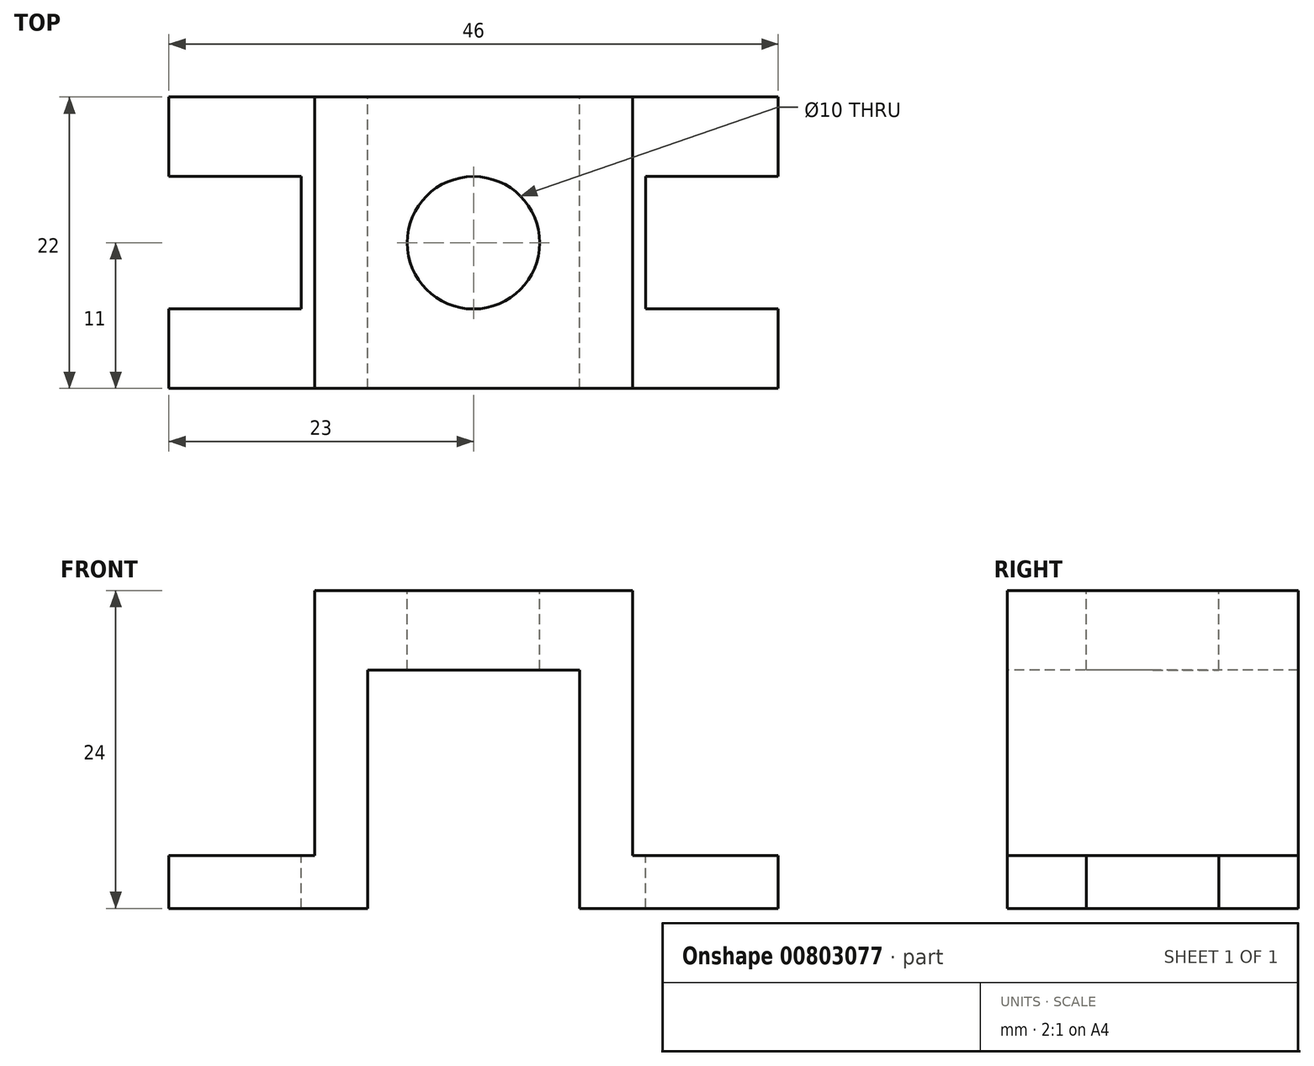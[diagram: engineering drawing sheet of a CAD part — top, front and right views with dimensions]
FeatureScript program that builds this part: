
annotation { "Feature Type Name" : "Feature", "Feature Type Description" : "" }
export const myFeature = defineFeature(function(context is Context, id is Id, definition is map)
    precondition{}
    {
        {
            var Q0;
            Q0=qCreatedBy(makeId("Front.planeOp"),FACE);
            var sketch = newSketch(context, id + "F0", { "sketchPlane" : qUnion([Q0])});
            skLineSegment(sketch, "E0.bottom", {"start": v(23, 12) * mm, "end": v(-23, 12) * mm});
            skLineSegment(sketch, "E0.top", {"start": v(23, -12) * mm, "end": v(-23, -12) * mm});
            skLineSegment(sketch, "E0.left", {"start": v(23, 12) * mm, "end": v(23, -12) * mm});
            skLineSegment(sketch, "E0.right", {"start": v(-23, 12) * mm, "end": v(-23, -12) * mm});
            skPoint(sketch, "E0.middle", {"position": v(0, 0) * mm});
            skSolve(sketch);
        }
        {
            var Q0;
            Q0 = qSketchRegion(id + "F0", true);
            extrude(context, id + "F1", {"entities" : qUnion([Q0]), "depth" : 11 * mm, "offsetDistance" : 25 * mm, "hasSecondDirection" : true, "secondDirectionOppositeDirection" : true, "secondDirectionDepth" : 11 * mm});
        }
        {
            var Q0;
            Q0=qCreatedBy(makeId("Front.planeOp"),FACE);
            var sketch = newSketch(context, id + "F2", { "sketchPlane" : qUnion([Q0])});
            skLineSegment(sketch, "E1.bottom", {"start": v(-8, 6) * mm, "end": v(8, 6) * mm});
            skLineSegment(sketch, "E1.top", {"start": v(-8, -21.9) * mm, "end": v(8, -21.9) * mm});
            skLineSegment(sketch, "E1.left", {"start": v(-8, 6) * mm, "end": v(-8, -21.9) * mm});
            skLineSegment(sketch, "E1.right", {"start": v(8, 6) * mm, "end": v(8, -21.9) * mm});
            skLineSegment(sketch, "E2.bottom", {"start": v(-28.7, 14) * mm, "end": v(-12, 14) * mm});
            skLineSegment(sketch, "E2.top", {"start": v(-28.7, -8) * mm, "end": v(-12, -8) * mm});
            skLineSegment(sketch, "E2.left", {"start": v(-28.7, 14) * mm, "end": v(-28.7, -8) * mm});
            skLineSegment(sketch, "E2.right", {"start": v(-12, 14) * mm, "end": v(-12, -8) * mm});
            skLineSegment(sketch, "E3.MirrorCS", {"start": v(12, 14) * mm, "end": v(12, -8) * mm});
            skLineSegment(sketch, "E4.MirrorCS", {"start": v(28.7, -8) * mm, "end": v(12, -8) * mm});
            skLineSegment(sketch, "E5.MirrorCS", {"start": v(28.7, 14) * mm, "end": v(28.7, -8) * mm});
            skLineSegment(sketch, "E6.MirrorCS", {"start": v(28.7, 14) * mm, "end": v(12, 14) * mm});
            skSolve(sketch);
        }
        {
            var Q0;
            Q0=makeQuery(id+"F2.imprint","IMPRINT",FACE,{"disambiguationData":[TD([[makeQuery(id+"F2.imprint","IMPRINT",EDGE,{"derivedFrom":sQuery(id+"F2.wireOp",EDGE,"E2.bottom")}),-1.0]])]});
            var Q1;
            Q1=makeQuery(id+"F2.imprint","IMPRINT",FACE,{"disambiguationData":[TD([[makeQuery(id+"F2.imprint","IMPRINT",EDGE,{"derivedFrom":sQuery(id+"F2.wireOp",EDGE,"E3.MirrorCS")}),1.0]])]});
            var Q2;
            Q2=makeQuery(id+"F2.imprint","IMPRINT",FACE,{"disambiguationData":[TD([[makeQuery(id+"F2.imprint","IMPRINT",EDGE,{"derivedFrom":sQuery(id+"F2.wireOp",EDGE,"E1.bottom")}),-1.0]])]});
            extrude(context, id + "F3", {"entities" : qUnion([Q0, Q1, Q2]), "operationType" : NewBodyOperationType.REMOVE, "oppositeDirection" : true, "depth" : 25 * mm, "offsetDistance" : 25 * mm, "hasSecondDirection" : true, "secondDirectionOppositeDirection" : false, "secondDirectionDepth" : 25 * mm});
        }
        {
            var Q0;
            Q0=makeQuery(id+"F3.boolean.opBoolean","COPY",FACE,{"derivedFrom":makeQuery(id+"F3.opExtrude","SWEPT_FACE",FACE,{"disambiguationData":[OSD([sQuery(id+"F2.wireOp",EDGE,"E2.top")])]})});
            var sketch = newSketch(context, id + "F4", { "sketchPlane" : qUnion([Q0])});
            skLineSegment(sketch, "E7.bottom", {"start": v(-26.83, 5) * mm, "end": v(-13, 5) * mm});
            skLineSegment(sketch, "E7.top", {"start": v(-26.83, -5) * mm, "end": v(-13, -5) * mm});
            skLineSegment(sketch, "E7.left", {"start": v(-26.83, 5) * mm, "end": v(-26.83, -5) * mm});
            skLineSegment(sketch, "E7.right", {"start": v(-13, 5) * mm, "end": v(-13, -5) * mm});
            skLineSegment(sketch, "E8.MirrorCS", {"start": v(13, 5) * mm, "end": v(13, -5) * mm});
            skLineSegment(sketch, "E9.MirrorCS", {"start": v(26.83, 5) * mm, "end": v(26.83, -5) * mm});
            skLineSegment(sketch, "E10.MirrorCS", {"start": v(26.83, 5) * mm, "end": v(13, 5) * mm});
            skLineSegment(sketch, "E11.MirrorCS", {"start": v(26.83, -5) * mm, "end": v(13, -5) * mm});
            skSolve(sketch);
        }
        {
            var Q0;
            {var subQ0=sQuery(id+"F4.wireOp",EDGE,"E7.right");Q0=makeQuery(id+"F4.imprint","IMPRINT",FACE,{"disambiguationData":[TD([[makeQuery(id+"F4.imprint","IMPRINT",EDGE,{"derivedFrom":subQ0}),-1.0]])]});}
            var Q1;
            Q1=makeQuery(id+"F4.imprint","IMPRINT",FACE,{"disambiguationData":[TD([[makeQuery(id+"F4.imprint","IMPRINT",EDGE,{"derivedFrom":sQuery(id+"F4.wireOp",EDGE,"E8.MirrorCS")}),1.0]])]});
            var Q2;
            {var subQ0=sQuery(id+"F4.wireOp",EDGE,"E7.left");Q2=makeQuery(id+"F4.imprint","IMPRINT",FACE,{"disambiguationData":[TD([[makeQuery(id+"F4.imprint","IMPRINT",EDGE,{"derivedFrom":subQ0}),1.0]])]});}
            extrude(context, id + "F5", {"entities" : qUnion([Q0, Q1, Q2]), "operationType" : NewBodyOperationType.REMOVE, "oppositeDirection" : true, "depth" : 25 * mm, "offsetDistance" : 25 * mm});
        }
        {
            var Q0;
            Q0=makeQuery(id+"F1.opExtrude","SWEPT_FACE",FACE,{"disambiguationData":[OSD([sQuery(id+"F0.wireOp",EDGE,"E0.bottom")])]});
            var sketch = newSketch(context, id + "F6", { "sketchPlane" : qUnion([Q0])});
            skCircle(sketch, "E12", {"center": v(0, 0) * mm, "radius": 5 * mm});
            skSolve(sketch);
        }
        {
            var Q0;
            Q0=makeQuery(id+"F6.imprint","IMPRINT",FACE,{"disambiguationData":[TD([[makeQuery(id+"F6.imprint","IMPRINT",EDGE,{"derivedFrom":sQuery(id+"F6.wireOp",EDGE,"E12")}),1.0]])]});
            extrude(context, id + "F7", {"entities" : qUnion([Q0]), "operationType" : NewBodyOperationType.REMOVE, "oppositeDirection" : true, "depth" : 10 * mm, "offsetDistance" : 25 * mm});
        }
    });
